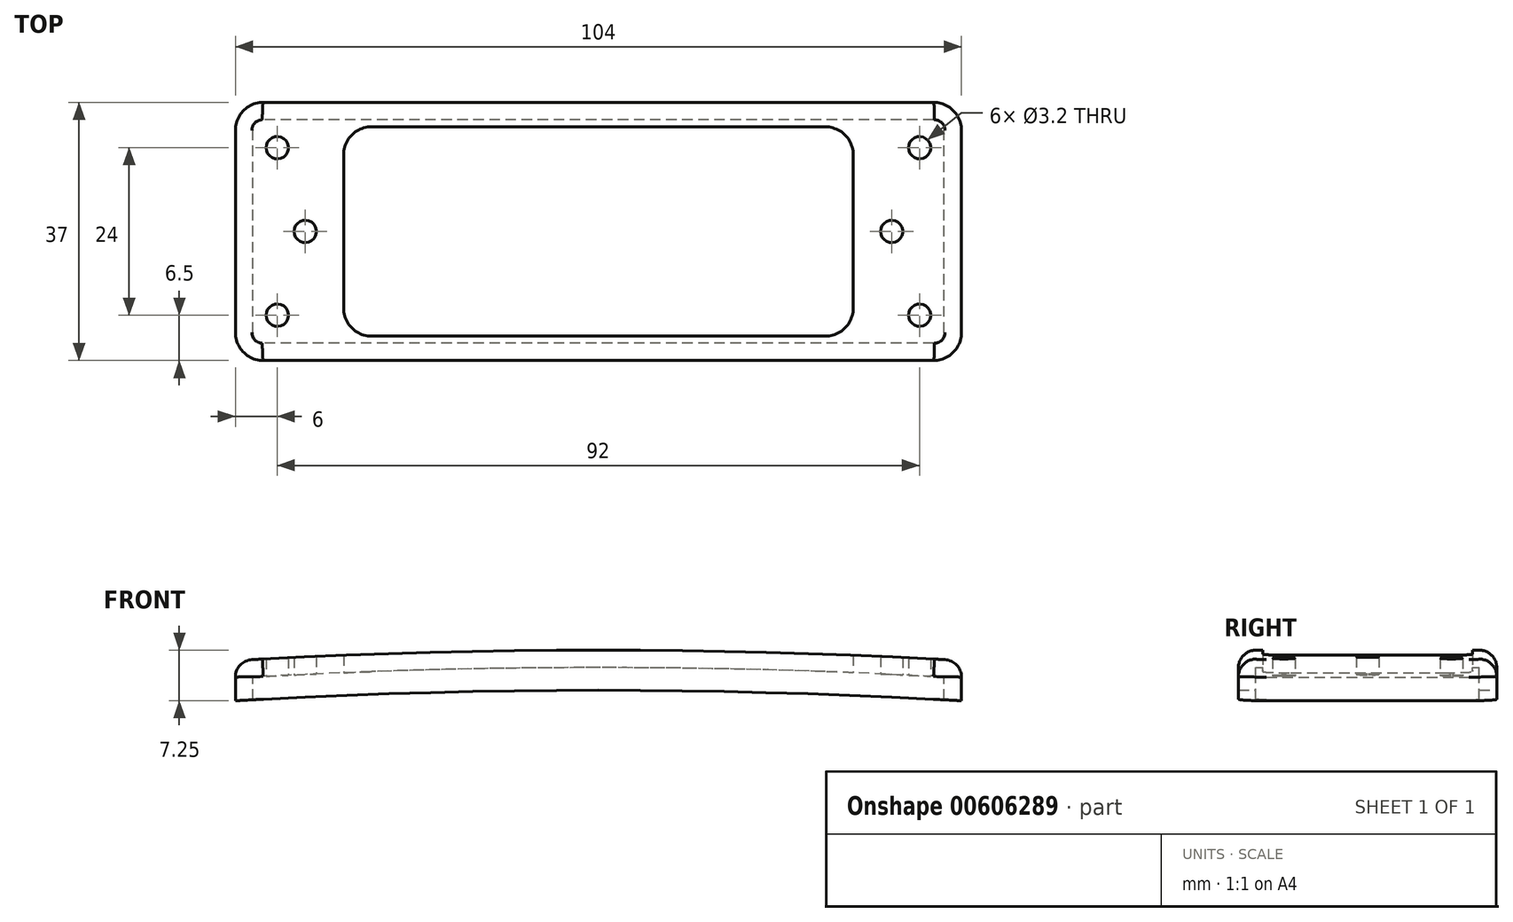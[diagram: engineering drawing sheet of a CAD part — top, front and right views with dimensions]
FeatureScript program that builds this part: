
annotation { "Feature Type Name" : "Feature", "Feature Type Description" : "" }
export const myFeature = defineFeature(function(context is Context, id is Id, definition is map)
    precondition{}
    {
        {
            var Q0;
            Q0=qCreatedBy(makeId("Front.planeOp"),FACE);
            var sketch = newSketch(context, id + "F0", { "sketchPlane" : qUnion([Q0])});
            skArc(sketch, "E0", {"start": v(52, 0) * mm, "mid": v(0, 1.5) * mm, "end": v(-52, 0) * mm});
            skLineSegment(sketch, "E1", {"start": v(-52, 0) * mm, "end": v(52, 0) * mm, "construction": true});
            skPoint(sketch, "E2", {"position": v(0, 0) * mm});
            skLineSegment(sketch, "E3", {"start": v(-52, 0) * mm, "end": v(-52, 5.76) * mm});
            skLineSegment(sketch, "E4", {"start": v(52, 0) * mm, "end": v(52, 5.76) * mm});
            skArc(sketch, "E5.0", {"start": v(52, 5.76) * mm, "mid": v(0, 7.25) * mm, "end": v(-52, 5.76) * mm});
            skSolve(sketch);
        }
        {
            var Q0;
            Q0 = qSketchRegion(id + "F0", true);
            extrude(context, id + "F1", {"entities" : qUnion([Q0]), "endBound" : BoundingType.SYMMETRIC, "depth" : 37 * mm, "offsetDistance" : 25 * mm});
        }
        {
            var Q0;
            Q0=makeQuery(id+"F1.opExtrude","CAP_EDGE",EDGE,{"disambiguationData":[OSD([sQuery(id+"F0.wireOp",EDGE,"E3")])],"isStart":false});
            var Q1;
            Q1=makeQuery(id+"F1.opExtrude","CAP_EDGE",EDGE,{"disambiguationData":[OSD([sQuery(id+"F0.wireOp",EDGE,"E4")])],"isStart":false});
            var Q2;
            Q2=makeQuery(id+"F1.opExtrude","CAP_EDGE",EDGE,{"disambiguationData":[OSD([sQuery(id+"F0.wireOp",EDGE,"E4")])],"isStart":true});
            var Q3;
            Q3=makeQuery(id+"F1.opExtrude","CAP_EDGE",EDGE,{"disambiguationData":[OSD([sQuery(id+"F0.wireOp",EDGE,"E3")])],"isStart":true});
            fillet(context, id + "F2", {"entities" : qUnion([Q0, Q1, Q2, Q3]), "radius" : 4 * mm, "tangentPropagation" : true, "allowEdgeOverflow" : false});
        }
        {
            var Q0;
            Q0=makeQuery(id+"F1.opExtrude","SWEPT_FACE",FACE,{"disambiguationData":[OSD([sQuery(id+"F0.wireOp",EDGE,"E5.0")])]});
            fillet(context, id + "F3", {"entities" : qUnion([Q0]), "radius" : 2.5 * mm, "tangentPropagation" : true, "allowEdgeOverflow" : false});
        }
        {
            var Q0;
            Q0=makeQuery(id+"F1.opExtrude","SWEPT_FACE",FACE,{"disambiguationData":[OSD([sQuery(id+"F0.wireOp",EDGE,"E0")])]});
            shell(context, id + "F4", {"entities" : qUnion([Q0]), "thickness" : 2.5 * mm});
        }
        {
            var Q0;
            Q0=qCreatedBy(makeId("Top.planeOp"),FACE);
            var sketch = newSketch(context, id + "F5", { "sketchPlane" : qUnion([Q0])});
            skLineSegment(sketch, "E6.bottom", {"start": v(32.5, 15) * mm, "end": v(-32.5, 15) * mm});
            skLineSegment(sketch, "E6.top", {"start": v(32.5, -15) * mm, "end": v(-32.5, -15) * mm});
            skLineSegment(sketch, "E6.left", {"start": v(36.5, 11) * mm, "end": v(36.5, -11) * mm});
            skLineSegment(sketch, "E6.right", {"start": v(-36.5, 11) * mm, "end": v(-36.5, -11) * mm});
            skPoint(sketch, "E6.middle", {"position": v(0, 0) * mm});
            skPoint(sketch, "E7.visualSharp", {"position": v(-36.5, 15) * mm});
            skArc(sketch, "E7.filletArc", {"start": v(-32.5, 15) * mm, "mid": v(-35.33, 13.83) * mm, "end": v(-36.5, 11) * mm});
            skPoint(sketch, "E8.visualSharp", {"position": v(-36.5, -15) * mm});
            skArc(sketch, "E8.filletArc", {"start": v(-36.5, -11) * mm, "mid": v(-35.33, -13.83) * mm, "end": v(-32.5, -15) * mm});
            skPoint(sketch, "E9.visualSharp", {"position": v(36.5, -15) * mm});
            skArc(sketch, "E9.filletArc", {"start": v(32.5, -15) * mm, "mid": v(35.33, -13.83) * mm, "end": v(36.5, -11) * mm});
            skPoint(sketch, "E10.visualSharp", {"position": v(36.5, 15) * mm});
            skArc(sketch, "E10.filletArc", {"start": v(36.5, 11) * mm, "mid": v(35.33, 13.83) * mm, "end": v(32.5, 15) * mm});
            skSolve(sketch);
        }
        {
            var Q0;
            Q0 = qSketchRegion(id + "F5", true);
            extrude(context, id + "F6", {"entities" : qUnion([Q0]), "operationType" : NewBodyOperationType.REMOVE, "endBound" : BoundingType.THROUGH_ALL, "depth" : 25 * mm, "offsetDistance" : 25 * mm});
        }
        {
            var Q0;
            Q0=qCreatedBy(makeId("Top.planeOp"),FACE);
            var sketch = newSketch(context, id + "F7", { "sketchPlane" : qUnion([Q0])});
            skLineSegment(sketch, "E11", {"start": v(-42, 0) * mm, "end": v(42, 0) * mm, "construction": true});
            skLineSegment(sketch, "E12.bottom", {"start": v(46, 12) * mm, "end": v(-46, 12) * mm, "construction": true});
            skLineSegment(sketch, "E12.top", {"start": v(46, -12) * mm, "end": v(-46, -12) * mm, "construction": true});
            skLineSegment(sketch, "E12.left", {"start": v(46, 12) * mm, "end": v(46, -12) * mm, "construction": true});
            skLineSegment(sketch, "E12.right", {"start": v(-46, 12) * mm, "end": v(-46, -12) * mm, "construction": true});
            skPoint(sketch, "E12.middle", {"position": v(0, 0) * mm});
            skCircle(sketch, "E13", {"center": v(-46, 12) * mm, "radius": 1.6 * mm});
            skCircle(sketch, "E14", {"center": v(-42, 0) * mm, "radius": 1.6 * mm});
            skCircle(sketch, "E15", {"center": v(-46, -12) * mm, "radius": 1.6 * mm});
            skCircle(sketch, "E16", {"center": v(46, -12) * mm, "radius": 1.6 * mm});
            skCircle(sketch, "E17", {"center": v(42, 0) * mm, "radius": 1.6 * mm});
            skCircle(sketch, "E18", {"center": v(46, 12) * mm, "radius": 1.6 * mm});
            skSolve(sketch);
        }
        {
            var Q0;
            Q0 = qSketchRegion(id + "F7", true);
            extrude(context, id + "F8", {"entities" : qUnion([Q0]), "operationType" : NewBodyOperationType.REMOVE, "endBound" : BoundingType.THROUGH_ALL, "depth" : 25 * mm, "offsetDistance" : 25 * mm});
        }
    });
